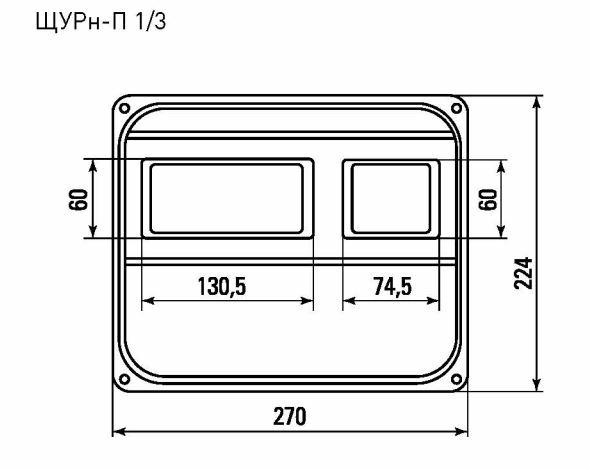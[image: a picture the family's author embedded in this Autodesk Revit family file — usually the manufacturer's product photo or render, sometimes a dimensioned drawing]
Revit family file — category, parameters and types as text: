
# Revit family: EKF_EE_ЩМП_IP31_PROxima
name_source: partatom
category: Электрооборудование
units: mm (PartAtom-declared; Revit-internal decimal feet)

## family parameters
Всегда вертикально = Да
На основе рабочей плоскости = Нет
Общий = Нет
При загрузке вырезать с полостями = Нет
Размер круглого соединителя = Использовать диаметр
Тип детали = Силовой щит
Точка расчета площади = Да

## types (22) — shared parameters
ADSK_Единица измерения = компл.
ADSK_Завод-изготовитель = EKF
ADSK_Классификация нагрузок = Прочее
ADSK_Количество = 1
ADSK_Количество фаз = 3
ADSK_Коэффициент мощности = 1
ADSK_Материал = RAL 7035_Сталь
ADSK_Напряжение = 400 В
ADSK_Номинальная мощность = 0 Вт
ADSK_Полная мощность = 0 В·А
ADSK_Ток = 125 А
Изготовитель = EKF
Серия номенклатуры = Basic
Степень защиты IP = IP54
ТВ = EKF
Тип установки = Навесной
zero-valued in all types: Количество DIN-реек, Количество модулей на DIN-рейке, Максимальное количество модулей

## per-type parameters (varying)
| type | ADSK_Код изделия | ADSK_Марка | ADSK_Масса | ADSK_Наименование | ADSK_Обозначение | ADSK_Размер_Высота | ADSK_Размер_Глубина | ADSK_Размер_Ширина | Описание | Тип |
| ЩМП-100.65.30 (ЩРНМ-5) IP31 EKF PROxima | mb22-5 | ЩМП-100.65.30 (ЩРНМ-5) IP31 | 29.95 | Щит с монтажной панелью ЩМП-100.65.30 (ЩРНМ-5) IP31 EKF PROxima | ЩМП-100.65.30 (ЩРНМ-5) IP31 | 1000 мм | 300 мм | 650 мм | Щит с монтажной панелью ЩМП-100.65.30 (ЩРНМ-5) IP31 EKF PROxima | 79 мм |
| ЩМП-120.75.30 (ЩРНМ-6) IP31 EKF PROxima | mb22-6 | ЩМП-120.75.30 (ЩРНМ-6) IP31 | 39.73 | Щит с монтажной панелью ЩМП-120.75.30 (ЩРНМ-6) IP31 EKF PROxima | ЩМП-120.75.30 (ЩРНМ-6) IP31 | 1200 мм | 300 мм | 750 мм | Щит с монтажной панелью ЩМП-120.75.30 (ЩРНМ-6) IP31 EKF PROxima | 80 мм |
| ЩМП-132.75.30 (ЩРНМ-7) IP31 EKF PROxima | mb22-7 | ЩМП-132.75.30 (ЩРНМ-7) IP31 | 40.25 | Щит с монтажной панелью ЩМП-132.75.30 (ЩРНМ-7) IP31 EKF PROxima | ЩМП-132.75.30 (ЩРНМ-7) IP31 | 1320 мм | 300 мм | 750 мм | Щит с монтажной панелью ЩМП-132.75.30 (ЩРНМ-7) IP31 EKF PROxima | 81 мм |
| ЩМП-90.70.26 (ЩМП-08) IP31 EKF PROxima | mb22-08 | ЩМП- 90.70.26 (ЩМП-08) IP31 | 24.1 | Щит с монтажной панелью ЩМП- 90.70.26 (ЩМП-08) IP31 EKF PROxima | ЩМП- 90.70.26 (ЩМП-08) IP31 | 900 мм | 260 мм | 700 мм | Щит с монтажной панелью ЩМП- 90.70.26 (ЩМП-08) IP31 EKF PROxima | 78 мм |
| ЩМП-80.60.25 (ЩРНМ-4) IP31 EKF PROxima | mb22-4 | ЩМП- 80.60.25 (ЩРНМ-4) IP31 | 25.1 | Щит с монтажной панелью ЩМП- 80.60.25 (ЩРНМ-4) IP31 EKF PROxima | ЩМП- 80.60.25 (ЩРНМ-4) IP31 | 800 мм | 250 мм | 600 мм | Щит с монтажной панелью ЩМП- 80.60.25 (ЩРНМ-4) IP31 EKF PROxima | 77 мм |
| ЩМП-70.50.21 (ЩМП-07) IP31 EKF PROxima | mb22-07 | ЩМП- 70.50.21. (ЩМП-07) IP31 | 13.8 | Щит с монтажной панелью ЩМП- 70.50.21. (ЩМП-07) IP31 EKF PROxima | ЩМП- 70.50.21. (ЩМП-07) IP31 | 700 мм | 210 мм | 500 мм | Щит с монтажной панелью ЩМП- 70.50.21. (ЩМП-07) IP31 EKF PROxima | 76 мм |
| ЩМП-65.50.22 (ЩРНМ-3) IP31 EKF PROxima | mb22-3 | ЩМП- 65.50.22 (ЩРНМ-3) IP31 | 12.43 | Щит с монтажной панелью ЩМП- 65.50.22 (ЩРНМ-3) IP31 EKF PROxima | ЩМП- 65.50.22 (ЩРНМ-3) IP31 | 650 мм | 220 мм | 500 мм | Щит с монтажной панелью ЩМП- 65.50.22 (ЩРНМ-3) IP31 EKF PROxima | 75 мм |
| ЩМП-65.50.15 IP31 EKF PROxima | mb22-31 | ЩМП- 65.50.15 IP31 | 10.92 | Щит с монтажной панелью ЩМП- 65.50.15 IP31 EKF PROxima | ЩМП- 65.50.15 IP31 | 650 мм | 150 мм | 500 мм | Щит с монтажной панелью ЩМП- 65.50.15 IP31 EKF PROxima | 74 мм |
| ЩМП-60.60.40 (ЩМП-12) IP31 EKF PROxima | mb22-12 | ЩМП- 60.60.40 (ЩМП-12) IP31 | 16.3 | Щит с монтажной панелью ЩМП- 60.60.40 (ЩМП-12) IP31 EKF PROxima | ЩМП- 60.60.40 (ЩМП-12) IP31 | 600 мм | 400 мм | 600 мм | Щит с монтажной панелью ЩМП- 60.60.40 (ЩМП-12) IP31 EKF PROxima | 73 мм |
| ЩМП-60.40.40 (ЩМП-11) IP31 EKF PROxima | mb22-11 | ЩМП- 60.40.40 (ЩМП-11) IP31 | 12.14 | Щит с монтажной панелью ЩМП- 60.40.40 (ЩМП-11) IP31 EKF PROxima | ЩМП- 60.40.40 (ЩМП-11) IP31 | 600 мм | 400 мм | 400 мм | Щит с монтажной панелью ЩМП- 60.40.40 (ЩМП-11) IP31 EKF PROxima | 72 мм |
| ЩМП-60.40.21 (ЩМП-09) IP31 EKF PROxima | mb22-09 | ЩМП- 60.40.21 (ЩМП-09) IP31 | 3.23 | Щит с монтажной панелью ЩМП- 60.40.21 (ЩМП-09) IP31 EKF PROxima | ЩМП- 60.40.21 (ЩМП-09) IP31 | 600 мм | 210 мм | 400 мм | Щит с монтажной панелью ЩМП- 60.40.21 (ЩМП-09) IP31 EKF PROxima | 71 мм |
| ЩМП-50.40.22 (ЩРНМ-2) IP31 EKF PROxima | mb22-2 | ЩМП- 50.40.22 (ЩРНМ-2) IP31 | 8.05 | Щит с монтажной панелью ЩМП- 50.40.22 (ЩРНМ-2) IP31 EKF PROxima | ЩМП- 50.40.22 (ЩРНМ-2) IP31 | 500 мм | 220 мм | 400 мм | Щит с монтажной панелью ЩМП- 50.40.22 (ЩРНМ-2) IP31 EKF PROxima | 70 мм |
| ЩМП-50.40.17 (ЩМП-06) IP31 EKF PROxima | mb22-06 | ЩМП- 50.40.17 (ЩМП-06) IP31 | 7.2 | Щит с монтажной панелью ЩМП- 50.40.17 (ЩМП-06) IP31 EKF PROxima | ЩМП- 50.40.17 (ЩМП-06) IP31 | 500 мм | 170 мм | 400 мм | Щит с монтажной панелью ЩМП- 50.40.17 (ЩМП-06) IP31 EKF PROxima | 69 мм |
| ЩМП-41.21.14 (ЩМП-01) IP31 EKF PROxima | mb22-01 | ЩМП- 41.21.14 (ЩМП-01) IP31 | 3.34 | Щит с монтажной панелью ЩМП- 41.21.14 (ЩМП-01) IP31 EKF PROxima | ЩМП- 41.21.14 (ЩМП-01) IP31 | 410 мм | 140 мм | 210 мм | Щит с монтажной панелью ЩМП- 41.21.14 (ЩМП-01) IP31 EKF PROxima | 68 мм |
| ЩМП-40.40.30 (ЩМП-10) IP31 EKF PROxima | mb22-10 | ЩМП- 40.40.30 (ЩМП-10) IP31 | 7.62 | Щит с монтажной панелью ЩМП- 40.40.30 (ЩМП-10) IP31 EKF PROxima | ЩМП- 40.40.30 (ЩМП-10) IP31 | 400 мм | 300 мм | 400 мм | Щит с монтажной панелью ЩМП- 40.40.30 (ЩМП-10) IP31 EKF PROxima | 67 мм |
| ЩМП-40.40.15 (ЩМП-05) IP31 EKF PROxima | mb22-05 | ЩМП- 40.40.15 (ЩМП-05) IP31 | 5.9 | Щит с монтажной панелью ЩМП- 40.40.15 (ЩМП-05) IP31 EKF PROxima | ЩМП- 40.40.15 (ЩМП-05) IP31 | 400 мм | 150 мм | 400 мм | Щит с монтажной панелью ЩМП- 40.40.15 (ЩМП-05) IP31 EKF PROxima | 66 мм |
| ЩМП-40.30.22 (ЩРНМ-1) IP31 EKF PROxima | mb22-1 | ЩМП- 40.30.22 (ЩРНМ-1) IP31 | 5.4 | Щит с монтажной панелью ЩМП- 40.30.22 (ЩРНМ-1) IP31 EKF PROxima | ЩМП- 40.30.22 (ЩРНМ-1) IP31 | 400 мм | 220 мм | 300 мм | Щит с монтажной панелью ЩМП- 40.30.22 (ЩРНМ-1) IP31 EKF PROxima | 65 мм |
| ЩМП-40.30.15 (ЩМП-04) IP31 EKF PROxima | mb22-04 | ЩМП- 40.30.15 (ЩМП-04) IP31 | 4.8 | Щит с монтажной панелью ЩМП- 40.30.15 (ЩМП-04) IP31 EKF PROxima | ЩМП- 40.30.15 (ЩМП-04) IP31 | 400 мм | 150 мм | 300 мм | Щит с монтажной панелью ЩМП- 40.30.15 (ЩМП-04) IP31 EKF PROxima | 64 мм |
| ЩМП-35.30.15 (ЩМП-03) IP31 EKF PROxima | mb22-03 | ЩМП- 35.30.15 (ЩМП-03) IP31 | 3.92 | Щит с монтажной панелью ЩМП- 35.30.15 (ЩМП-03) IP31 EKF PROxima | ЩМП- 35.30.15 (ЩМП-03) IP31 | 350 мм | 150 мм | 300 мм | Щит с монтажной панелью ЩМП- 35.30.15 (ЩМП-03) IP31 EKF PROxima | 63 мм |
| ЩМП-30.21.14 (ЩМП-00) IP31 EKF PROxima | mb-22-000 | ЩМП- 30.21.14 IP31 | 2.8 | Щит с монтажной панелью ЩМП- 30.21.14 IP31 EKF PROxima | ЩМП- 30.21.14 IP31 | 300 мм | 140 мм | 210 мм | Щит с монтажной панелью ЩМП- 30.21.14 IP31 EKF PROxima | 62 мм |
| ЩМП-27.21.14 (ЩМП-00) IP31 EKF PROxima | mb22-00 | ЩМП- 27.21.14 (ЩМП-00) IP31 | 2.3 | Щит с монтажной панелью ЩМП- 27.21.14 (ЩМП-00) IP31 EKF PROxima | ЩМП- 27.21.14 (ЩМП-00) IP31 | 270 мм | 140 мм | 210 мм | Щит с монтажной панелью ЩМП- 27.21.14 (ЩМП-00) IP31 EKF PROxima | 61 мм |
| ЩМП-25.30.14 (ЩМП-02) IP31 EKF PROxima | mb22-02 | ЩМП- 25.30.14 (ЩМП-02) IP31 | 2.88 | Щит с монтажной панелью ЩМП- 25.30.14 (ЩМП-02) IP31EKF PROxima | ЩМП- 25.30.14 (ЩМП-02) IP31 | 250 мм | 140 мм | 300 мм | Щит с монтажной панелью ЩМП- 25.30.14 (ЩМП-02) IP31EKF PROxima | 60 мм |
